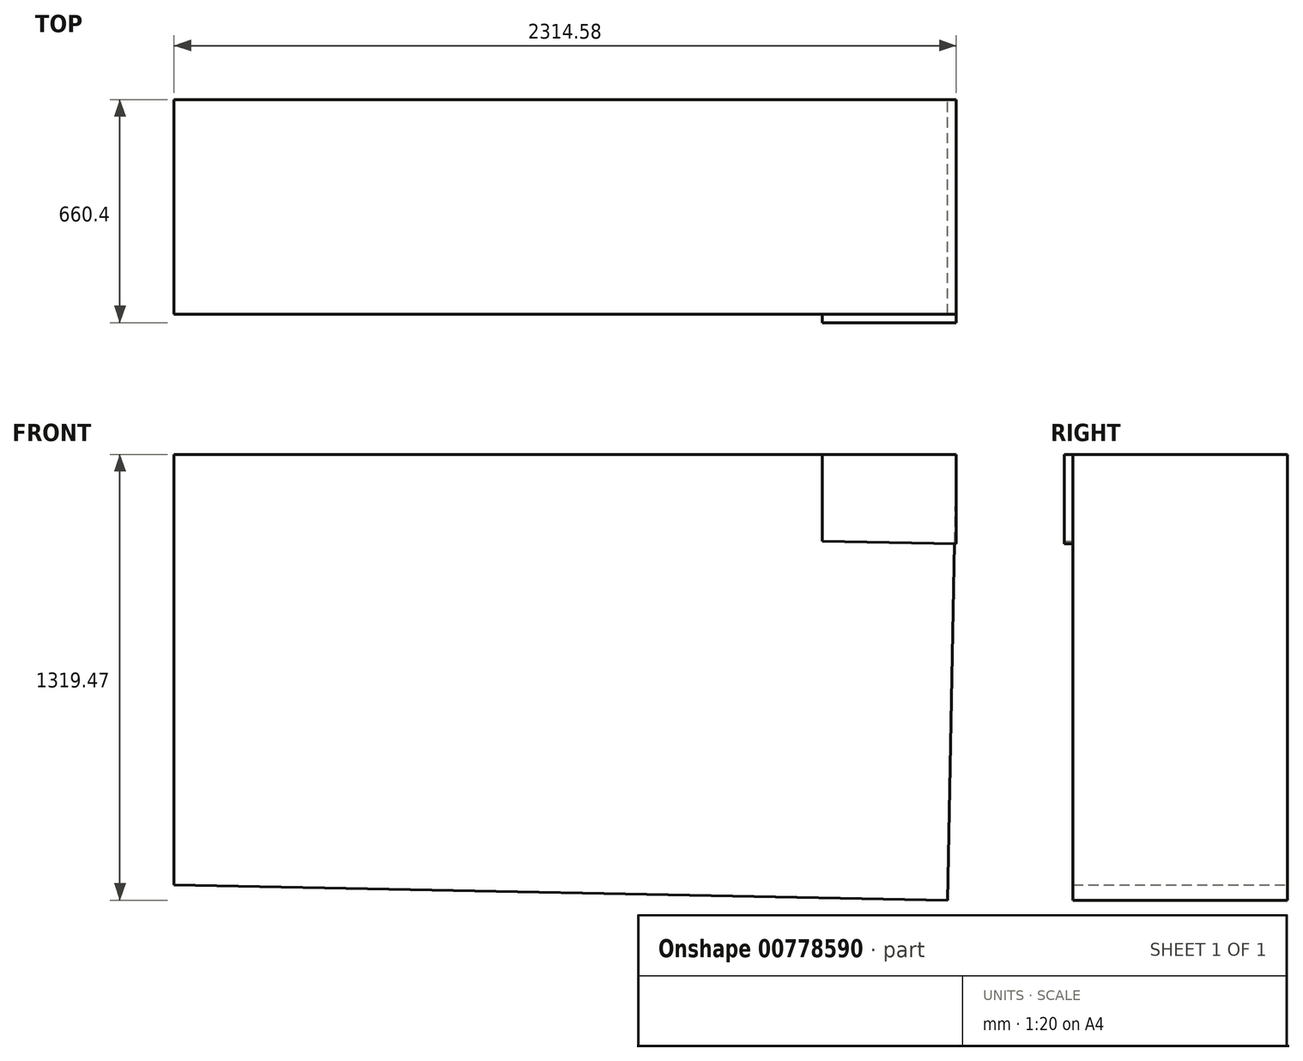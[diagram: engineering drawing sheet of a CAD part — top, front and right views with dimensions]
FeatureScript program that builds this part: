
annotation { "Feature Type Name" : "Feature", "Feature Type Description" : "" }
export const myFeature = defineFeature(function(context is Context, id is Id, definition is map)
    precondition{}
    {
        {
            var Q0;
            Q0=qCreatedBy(makeId("Front.planeOp"),FACE);
            var sketch = newSketch(context, id + "F0", { "sketchPlane" : qUnion([Q0])});
            skLineSegment(sketch, "E0", {"start": v(-329.92, 1274) * mm, "end": v(-329.92, 0) * mm});
            skLineSegment(sketch, "E1", {"start": v(-329.92, 0) * mm, "end": v(1958.99, -45.47) * mm});
            skLineSegment(sketch, "E2", {"start": v(-329.92, 1274) * mm, "end": v(1984.66, 1274) * mm});
            skLineSegment(sketch, "E3", {"start": v(1984.66, 1274) * mm, "end": v(1958.99, -45.47) * mm});
            skSolve(sketch);
        }
        {
            var Q0;
            Q0 = qSketchRegion(id + "F0", true);
            extrude(context, id + "F1", {"entities" : qUnion([Q0]), "depth" : 635 * mm, "offsetDistance" : 25.4 * mm});
        }
        {
            var Q0;
            Q0=makeQuery(id+"F1.opExtrude","CAP_FACE",FACE,{"disambiguationData":[OSD([sQuery(id+"F0.wireOp",EDGE,"E0"),sQuery(id+"F0.wireOp",EDGE,"E1"),sQuery(id+"F0.wireOp",EDGE,"E2"),sQuery(id+"F0.wireOp",EDGE,"E3")])],"isStart":false});
            var sketch = newSketch(context, id + "F2", { "sketchPlane" : qUnion([Q0])});
            skLineSegment(sketch, "E4", {"start": v(1984.66, 1274) * mm, "end": v(1588.27, 1274) * mm});
            skLineSegment(sketch, "E5", {"start": v(1588.27, 1274) * mm, "end": v(1588.27, 1016.6) * mm});
            skLineSegment(sketch, "E6", {"start": v(1588.27, 1016.6) * mm, "end": v(1984.66, 1008.9) * mm});
            skLineSegment(sketch, "E7", {"start": v(1588.27, 1274) * mm, "end": v(1984.66, 1701.77) * mm});
            skLineSegment(sketch, "E8", {"start": v(1977.62, 1704.52) * mm, "end": v(2341.98, 1697.44) * mm});
            skLineSegment(sketch, "E9", {"start": v(2341.94, 1695.32) * mm, "end": v(1984.66, 1274) * mm});
            skLineSegment(sketch, "E10", {"start": v(1984.66, 1274) * mm, "end": v(1984.66, 1008.9) * mm});
            skLineSegment(sketch, "E11", {"start": v(1992.45, 1008.25) * mm, "end": v(2340.21, 1402.4) * mm});
            skSolve(sketch);
        }
        {
            var Q0;
            Q0 = qSketchRegion(id + "F2", true);
            extrude(context, id + "F3", {"entities" : qUnion([Q0]), "depth" : 25.4 * mm, "offsetDistance" : 25.4 * mm});
        }
    });
